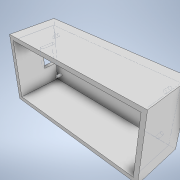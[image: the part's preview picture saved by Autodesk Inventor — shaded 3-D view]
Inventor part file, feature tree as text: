
AUTODESK INVENTOR PART (.ipt)
format: ipt  version: 2020.1 (Build 241239000, 239)  size: 132,608 bytes
history: native  units: mm
features: extrude x3, sketch x3, shell x1
ambient origin geometry x8: Origin, YZ Plane, XZ Plane, XY Plane, X Axis, Y Axis, Z Axis, Center Point
bodies: Solid1 (feature_tree)
feature tree (7):
  extrude  "Extrusion1"  Depth=32.0mm
  shell  "Shell1"  Thickness=23.0mm
  extrude  "Extrusion2"  Depth=5.0mm
  extrude  "Extrusion3"  Depth=10.0mm
  sketch  "Sketch1"  dims[d0=68.0mm d1=32.0mm d2=23.0mm d3=0.0mm]
  sketch  "Sketch5"  dims[d4=2.0mm d5=5.0mm]
  sketch  "Sketch6"  dims[d6=16.0mm d7=10.25mm d8=57.5mm d9=20.5mm d10=1.5mm d11=1.5mm d12=1.5mm d13=1.5mm d14=3.0mm d15=0.0mm d16=5.0mm d17=7.0mm d18=10.0mm d19=10.0mm d20=0.0mm]
